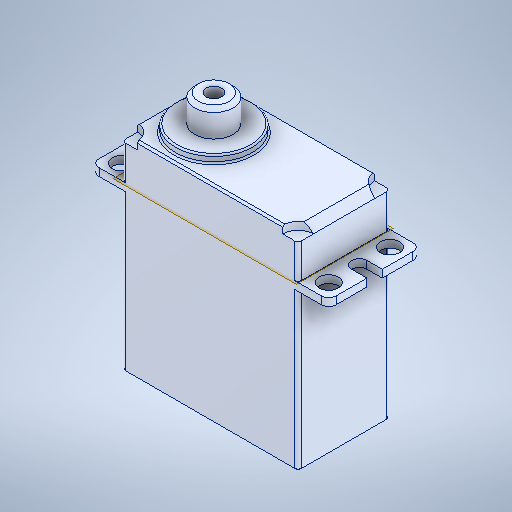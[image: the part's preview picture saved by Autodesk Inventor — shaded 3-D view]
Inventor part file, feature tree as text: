
AUTODESK INVENTOR PART (.ipt)
format: ipt  version: 2025.2 (Build 292293000, 293)  size: 331,264 bytes
history: native  units: in
note: dims shown in document units (in); Inventor stores cm internally (conversion verified against a paired STEP export)
features: other x1, chamfer x1
ambient origin geometry x8: Origin, YZ Plane, XZ Plane, XY Plane, X Axis, Y Axis, Z Axis, Center Point
bodies: Solid1 (feature_tree)
feature tree (2):
  other  "Plane1"
  chamfer  "Chamfer3"  [1 undecoded]
note: 1 required parameter value undecoded (feature->parameter linkage not recoverable at this tier; creation-order binding heuristic only, values carry confidence <= 0.55)
